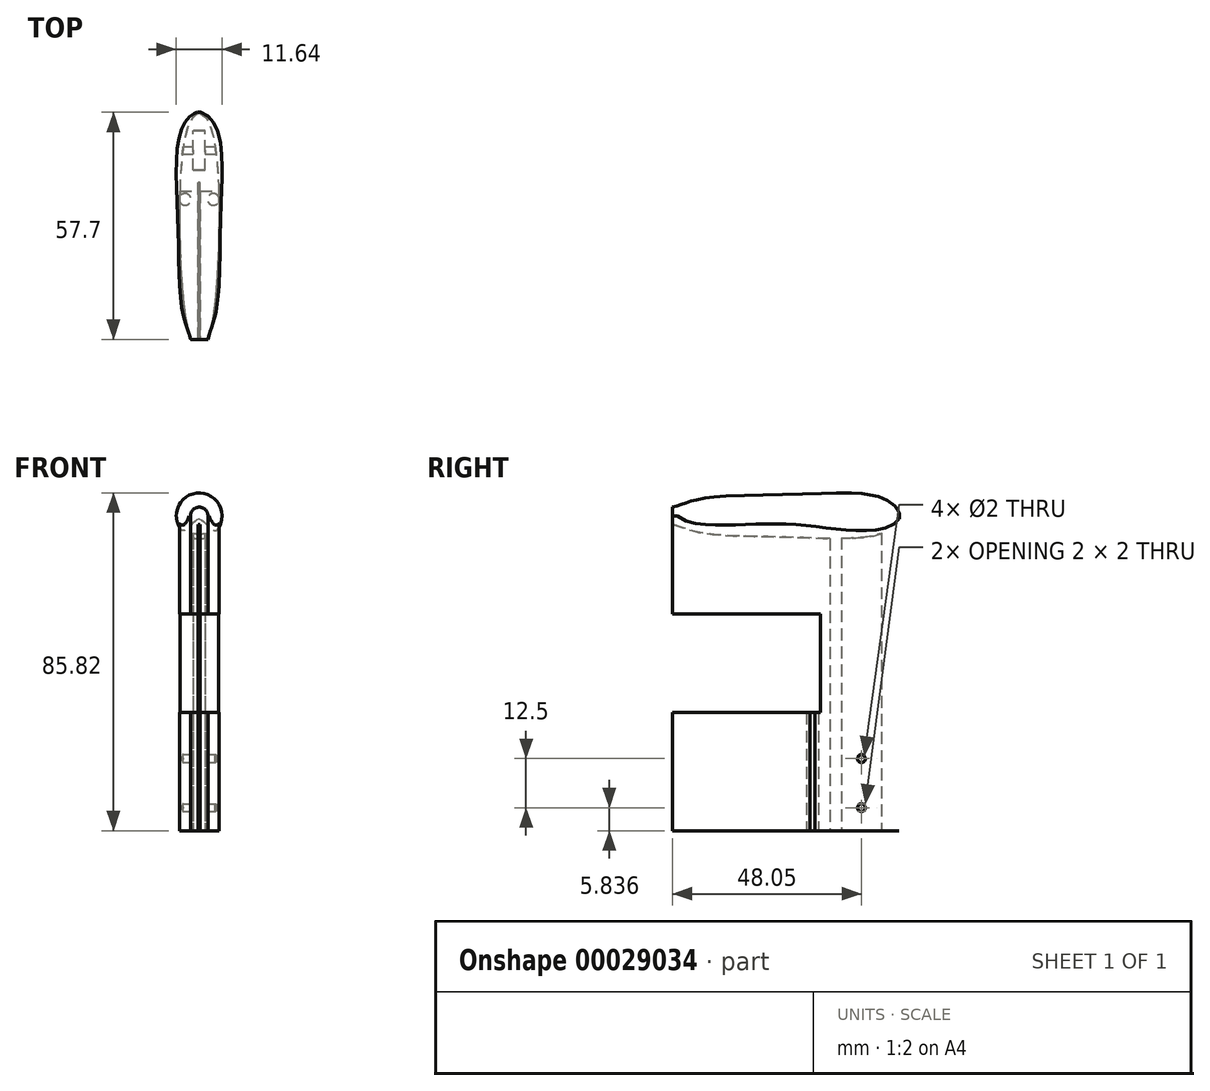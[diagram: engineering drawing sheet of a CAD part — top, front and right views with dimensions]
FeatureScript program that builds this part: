
annotation { "Feature Type Name" : "Feature", "Feature Type Description" : "" }
export const myFeature = defineFeature(function(context is Context, id is Id, definition is map)
    precondition{}
    {
        {
            var Q0;
            Q0=qCreatedBy(makeId("Top.planeOp"),FACE);
            var sketch = newSketch(context, id + "F0", { "sketchPlane" : qUnion([Q0])});
            skLineSegment(sketch, "E0", {"start": v(0, 90) * mm, "end": v(5, 90) * mm});
            skLineSegment(sketch, "E1", {"start": v(5, 90) * mm, "end": v(5, 10) * mm});
            skLineSegment(sketch, "E2", {"start": v(5, 10) * mm, "end": v(90, 10) * mm});
            skLineSegment(sketch, "E3", {"start": v(90, 10) * mm, "end": v(90, 0) * mm});
            skLineSegment(sketch, "E4", {"start": v(90, 0) * mm, "end": v(0, 0) * mm});
            skLineSegment(sketch, "E5.MirrorCS", {"start": v(0, 90) * mm, "end": v(-5, 90) * mm});
            skLineSegment(sketch, "E6.MirrorCS", {"start": v(-5, 90) * mm, "end": v(-5, 10) * mm});
            skLineSegment(sketch, "E7.MirrorCS", {"start": v(-5, 10) * mm, "end": v(-90, 10) * mm});
            skLineSegment(sketch, "E8.MirrorCS", {"start": v(-90, 10) * mm, "end": v(-90, 0) * mm});
            skLineSegment(sketch, "E9.MirrorCS", {"start": v(-90, 0) * mm, "end": v(0, 0) * mm});
            skSolve(sketch);
        }
        {
            var Q0;
            Q0=makeQuery(id+"F0.imprint","IMPRINT",FACE,{"disambiguationData":[TD([[makeQuery(id+"F0.imprint","IMPRINT",EDGE,{"derivedFrom":sQuery(id+"F0.wireOp",EDGE,"E0")}),-1.0]])]});
            extrude(context, id + "F1", {"entities" : qUnion([Q0]), "depth" : 10 * mm});
        }
        {
            var Q0;
            Q0=makeQuery(id+"F1.opExtrude","CAP_FACE",FACE,{"disambiguationData":[OSD([sQuery(id+"F0.wireOp",EDGE,"E0"),sQuery(id+"F0.wireOp",EDGE,"E1"),sQuery(id+"F0.wireOp",EDGE,"E2"),sQuery(id+"F0.wireOp",EDGE,"E3"),sQuery(id+"F0.wireOp",EDGE,"E4"),sQuery(id+"F0.wireOp",EDGE,"E5.MirrorCS"),sQuery(id+"F0.wireOp",EDGE,"E6.MirrorCS"),sQuery(id+"F0.wireOp",EDGE,"E7.MirrorCS"),sQuery(id+"F0.wireOp",EDGE,"E8.MirrorCS"),sQuery(id+"F0.wireOp",EDGE,"E9.MirrorCS")])],"isStart":false});
            var sketch = newSketch(context, id + "F2", { "sketchPlane" : qUnion([Q0])});
            skLineSegment(sketch, "E10.bottom", {"start": v(-5, 80) * mm, "end": v(5, 80) * mm});
            skLineSegment(sketch, "E10.top", {"start": v(-5, 70) * mm, "end": v(5, 70) * mm});
            skLineSegment(sketch, "E10.left", {"start": v(-5, 80) * mm, "end": v(-5, 70) * mm});
            skLineSegment(sketch, "E10.right", {"start": v(5, 80) * mm, "end": v(5, 70) * mm});
            skSolve(sketch);
        }
        {
            var Q0;
            Q0=makeQuery(id+"F2.imprint","IMPRINT",FACE,{"disambiguationData":[TD([[makeQuery(id+"F2.imprint","IMPRINT",EDGE,{"derivedFrom":sQuery(id+"F2.wireOp",EDGE,"E10.bottom")}),-1.0]])]});
            extrude(context, id + "F3", {"entities" : qUnion([Q0]), "operationType" : NewBodyOperationType.ADD, "depth" : 10 * mm});
        }
        {
            var Q0;
            {var subQ0=sQuery(id+"F0.wireOp",EDGE,"E1");var subQ1=sQuery(id+"F0.wireOp",EDGE,"E2");var subQ2=sQuery(id+"F0.wireOp",EDGE,"E3");var subQ3=sQuery(id+"F0.wireOp",EDGE,"E4");var subQ4=sQuery(id+"F0.wireOp",EDGE,"E6.MirrorCS");var subQ5=sQuery(id+"F0.wireOp",EDGE,"E7.MirrorCS");var subQ6=sQuery(id+"F0.wireOp",EDGE,"E8.MirrorCS");var subQ7=sQuery(id+"F0.wireOp",EDGE,"E9.MirrorCS");Q0=makeQuery(id+"F3.boolean.opBoolean","SPLIT",FACE,{"disambiguationData":[TD([makeQuery(id+"F1.opExtrude","SWEPT_FACE",FACE,{"disambiguationData":[OSD([subQ1])]})])],"derivedFrom":makeQuery(id+"F1.opExtrude","CAP_FACE",FACE,{"disambiguationData":[OSD([sQuery(id+"F0.wireOp",EDGE,"E0"),subQ0,subQ1,subQ2,subQ3,sQuery(id+"F0.wireOp",EDGE,"E5.MirrorCS"),subQ4,subQ5,subQ6,subQ7])],"isStart":false})});}
            var sketch = newSketch(context, id + "F4", { "sketchPlane" : qUnion([Q0])});
            skFitSpline(sketch, "E11", {"points": [v(0, 57.64) * mm, v(2.65, 54.58) * mm, v(5, 31.49) * mm, v(3.55, 6.02) * mm, v(2.2, 0) * mm], "startDerivative": vector(17.44, -0.09) * mm, "endDerivative": vector(-5.28, -21) * mm});
            skLineSegment(sketch, "E12", {"start": v(0, 57.64) * mm, "end": v(0, 24.79) * mm, "construction": true});
            skLineSegment(sketch, "E13", {"start": v(2.2, 0) * mm, "end": v(0.25, 0) * mm});
            skLineSegment(sketch, "E14", {"start": v(0.25, 0) * mm, "end": v(0.25, 40) * mm});
            skLineSegment(sketch, "E15", {"start": v(0.25, 40) * mm, "end": v(0, 40) * mm});
            skFitSpline(sketch, "E16.MirrorCS", {"points": [v(0, 57.64) * mm, v(-2.65, 54.58) * mm, v(-5, 31.49) * mm, v(-3.55, 6.02) * mm, v(-2.2, 0) * mm], "startDerivative": vector(-17.44, -0.09) * mm, "endDerivative": vector(5.28, -21) * mm});
            skLineSegment(sketch, "E17.MirrorCS", {"start": v(-0.25, 40) * mm, "end": v(0, 40) * mm});
            skLineSegment(sketch, "E18.MirrorCS", {"start": v(-0.25, 0) * mm, "end": v(-0.25, 40) * mm});
            skLineSegment(sketch, "E19.MirrorCS", {"start": v(-2.2, 0) * mm, "end": v(-0.25, 0) * mm});
            skLineSegment(sketch, "E20.rect.bottom", {"start": v(1.55, 43) * mm, "end": v(-1.55, 43) * mm});
            skLineSegment(sketch, "E20.rect.top", {"start": v(1.55, 53.1) * mm, "end": v(-1.55, 53.1) * mm});
            skLineSegment(sketch, "E20.rect.left", {"start": v(1.55, 43) * mm, "end": v(1.55, 53.1) * mm});
            skLineSegment(sketch, "E20.rect.right", {"start": v(-1.55, 43) * mm, "end": v(-1.55, 53.1) * mm});
            skPoint(sketch, "E20.rect.middle", {"position": v(0, 48.05) * mm});
            skSolve(sketch);
        }
        {
            var Q0;
            {var subQ19=sQuery(id+"F4.wireOp",EDGE,"E13");Q0=makeQuery(id+"F4.imprint","IMPRINT",FACE,{"disambiguationData":[TD([[makeQuery(id+"F4.imprint","IMPRINT",EDGE,{"derivedFrom":subQ19}),1.0]])]});}
            extrude(context, id + "F5", {"entities" : qUnion([Q0]), "operationType" : NewBodyOperationType.ADD, "depth" : 130 * mm});
        }
        {
            var Q0;
            Q0=qCreatedBy(makeId("Right.planeOp"),FACE);
            var sketch = newSketch(context, id + "F6", { "sketchPlane" : qUnion([Q0])});
            skLineSegment(sketch, "E21.bottom", {"start": v(-13.73, 90) * mm, "end": v(37.64, 90) * mm});
            skLineSegment(sketch, "E21.top", {"start": v(-13.73, 115) * mm, "end": v(37.64, 115) * mm});
            skLineSegment(sketch, "E21.left", {"start": v(-13.73, 90) * mm, "end": v(-13.73, 115) * mm});
            skLineSegment(sketch, "E21.right", {"start": v(37.64, 90) * mm, "end": v(37.64, 115) * mm});
            skSolve(sketch);
        }
        {
            var Q0;
            Q0=makeQuery(id+"F6.imprint","IMPRINT",FACE,{"disambiguationData":[TD([[makeQuery(id+"F6.imprint","IMPRINT",EDGE,{"derivedFrom":sQuery(id+"F6.wireOp",EDGE,"E21.bottom")}),1.0]])]});
            extrude(context, id + "F7", {"entities" : qUnion([Q0]), "operationType" : NewBodyOperationType.REMOVE, "endBound" : BoundingType.THROUGH_ALL, "oppositeDirection" : true, "depth" : 25 * mm, "hasSecondDirection" : true, "secondDirectionBound" : SecondDirectionBoundingType.THROUGH_ALL, "secondDirectionOppositeDirection" : false, "secondDirectionDepth" : 25 * mm});
        }
        {
            var Q0;
            Q0=qCreatedBy(makeId("Top.planeOp"),FACE);
            var sketch = newSketch(context, id + "F8", { "sketchPlane" : qUnion([Q0])});
            skLineSegment(sketch, "E22.rect.bottom", {"start": v(115.77, -104.9) * mm, "end": v(-115.77, -104.9) * mm});
            skLineSegment(sketch, "E22.rect.top", {"start": v(115.77, 104.9) * mm, "end": v(-115.77, 104.9) * mm});
            skLineSegment(sketch, "E22.rect.left", {"start": v(115.77, -104.9) * mm, "end": v(115.77, 104.9) * mm});
            skLineSegment(sketch, "E22.rect.right", {"start": v(-115.77, -104.9) * mm, "end": v(-115.77, 104.9) * mm});
            skPoint(sketch, "E22.rect.middle", {"position": v(0, 0) * mm});
            skSolve(sketch);
        }
        {
            var Q0;
            Q0=qSketchRegion(id+"F8",true);
            var Q1;
            Q1=makeQuery(id+"F3.opExtrude","CAP_FACE",FACE,{"disambiguationData":[OSD([sQuery(id+"F2.wireOp",EDGE,"E10.bottom"),sQuery(id+"F2.wireOp",EDGE,"E10.top"),sQuery(id+"F2.wireOp",EDGE,"E10.left"),sQuery(id+"F2.wireOp",EDGE,"E10.right")])],"isStart":false});
            extrude(context, id + "F9", {"entities" : qUnion([Q0]), "operationType" : NewBodyOperationType.REMOVE, "endBound" : BoundingType.UP_TO_SURFACE, "endBoundEntityFace" : qUnion([Q1]), "depth" : 25 * mm});
        }
        {
            var Q0;
            Q0=qCreatedBy(makeId("Right.planeOp"),FACE);
            var sketch = newSketch(context, id + "F10", { "sketchPlane" : qUnion([Q0])});
            skCircle(sketch, "E23", {"center": v(48.05, 28.34) * mm, "radius": 1 * mm});
            skCircle(sketch, "E24.1.0.0", {"center": v(48.05, 40.84) * mm, "radius": 1 * mm});
            skCircle(sketch, "E24.2.0.0", {"center": v(48.05, 53.34) * mm, "radius": 1 * mm});
            skLineSegment(sketch, "E24.direction1", {"start": v(48.05, 28.34) * mm, "end": v(48.05, 40.84) * mm, "construction": true});
            skCircle(sketch, "E25.0.3.0", {"center": v(48.05, 65.84) * mm, "radius": 1 * mm});
            skCircle(sketch, "E25.0.4.0", {"center": v(48.05, 78.34) * mm, "radius": 1 * mm});
            skSolve(sketch);
        }
        {
            var Q0;
            Q0=qSketchRegion(id+"F10",true);
            extrude(context, id + "F11", {"entities" : qUnion([Q0]), "operationType" : NewBodyOperationType.REMOVE, "endBound" : BoundingType.THROUGH_ALL, "oppositeDirection" : true, "depth" : 25 * mm, "hasSecondDirection" : true, "secondDirectionBound" : SecondDirectionBoundingType.THROUGH_ALL, "secondDirectionOppositeDirection" : false, "secondDirectionDepth" : 25 * mm});
        }
        {
            var Q0;
            Q0=qCreatedBy(makeId("Right.planeOp"),FACE);
            var sketch = newSketch(context, id + "F12", { "sketchPlane" : qUnion([Q0])});
            skLineSegment(sketch, "E26.bottom", {"start": v(78.93, -35.32) * mm, "end": v(-26.83, -35.32) * mm});
            skLineSegment(sketch, "E26.top", {"start": v(78.93, 60) * mm, "end": v(-26.83, 60) * mm});
            skLineSegment(sketch, "E26.left", {"start": v(78.93, -35.32) * mm, "end": v(78.93, 60) * mm});
            skLineSegment(sketch, "E26.right", {"start": v(-26.83, -35.32) * mm, "end": v(-26.83, 60) * mm});
            skSolve(sketch);
        }
        {
            var Q0;
            Q0=makeQuery(id+"F12.imprint","IMPRINT",FACE,{"disambiguationData":[TD([[makeQuery(id+"F12.imprint","IMPRINT",EDGE,{"derivedFrom":sQuery(id+"F12.wireOp",EDGE,"E26.bottom")}),-1.0]])]});
            extrude(context, id + "F13", {"entities" : qUnion([Q0]), "operationType" : NewBodyOperationType.REMOVE, "endBound" : BoundingType.SYMMETRIC, "oppositeDirection" : true, "depth" : 30 * mm});
        }
        {
            var Q0;
            Q0=makeQuery(id+"F13.boolean.opBoolean","COPY",FACE,{"derivedFrom":makeQuery(id+"F13.opExtrude","SWEPT_FACE",FACE,{"disambiguationData":[OSD([sQuery(id+"F12.wireOp",EDGE,"E26.top")])]})});
            var sketch = newSketch(context, id + "F14", { "sketchPlane" : qUnion([Q0])});
            skCircle(sketch, "E27", {"center": v(-3.6, -35.58) * mm, "radius": 1.5 * mm});
            skLineSegment(sketch, "E28", {"start": v(0, 0) * mm, "end": v(0, 2.54) * mm, "construction": true});
            skCircle(sketch, "E29.MirrorC", {"center": v(3.6, -35.58) * mm, "radius": 1.5 * mm});
            skSolve(sketch);
        }
        {
            var Q0;
            Q0 = qSketchRegion(id + "F14", true);
            extrude(context, id + "F15", {"entities" : qUnion([Q0]), "operationType" : NewBodyOperationType.REMOVE, "oppositeDirection" : true, "depth" : 30 * mm});
        }
        {
            var Q0;
            Q0=makeQuery(id+"F5.opExtrude","CAP_FACE",FACE,{"disambiguationData":[OSD([sQuery(id+"F4.wireOp",EDGE,"E11"),sQuery(id+"F4.wireOp",EDGE,"E13"),sQuery(id+"F4.wireOp",EDGE,"E14"),sQuery(id+"F4.wireOp",EDGE,"E15"),sQuery(id+"F4.wireOp",EDGE,"E16.MirrorCS"),sQuery(id+"F4.wireOp",EDGE,"E17.MirrorCS"),sQuery(id+"F4.wireOp",EDGE,"E18.MirrorCS"),sQuery(id+"F4.wireOp",EDGE,"E19.MirrorCS"),sQuery(id+"F4.wireOp",EDGE,"E20.rect.bottom"),sQuery(id+"F4.wireOp",EDGE,"E20.rect.top"),sQuery(id+"F4.wireOp",EDGE,"E20.rect.left"),sQuery(id+"F4.wireOp",EDGE,"E20.rect.right")])],"isStart":false});
            var sketch = newSketch(context, id + "F16", { "sketchPlane" : qUnion([Q0])});
            skFitSpline(sketch, "E30.0", {"points": [v(0, 57.64) * mm, v(-0.81, 57.64) * mm, v(-4.36, 53.8) * mm, v(-5.47, 31.15) * mm, v(-4.26, 7.04) * mm, v(-2.5, 1.21) * mm, v(-2.2, 0) * mm]});
            skLineSegment(sketch, "E30.1", {"start": v(-2.2, 0) * mm, "end": v(-0.25, 0) * mm});
            skLineSegment(sketch, "E31", {"start": v(-0.25, 0) * mm, "end": v(0, 0) * mm});
            skLineSegment(sketch, "E32", {"start": v(0, 0) * mm, "end": v(0, 57.64) * mm});
            skSolve(sketch);
        }
        {
            var Q0;
            Q0 = qSketchRegion(id + "F16", true);
            var Q1;
            Q1=sQuery(id+"F16.wireOp",EDGE,"E32");
            revolve(context, id + "F17", {"operationType" : NewBodyOperationType.ADD, "entities" : qUnion([Q0]), "axis" : qUnion([Q1]), "revolveType" : RevolveType.FULL});
        }
    });
